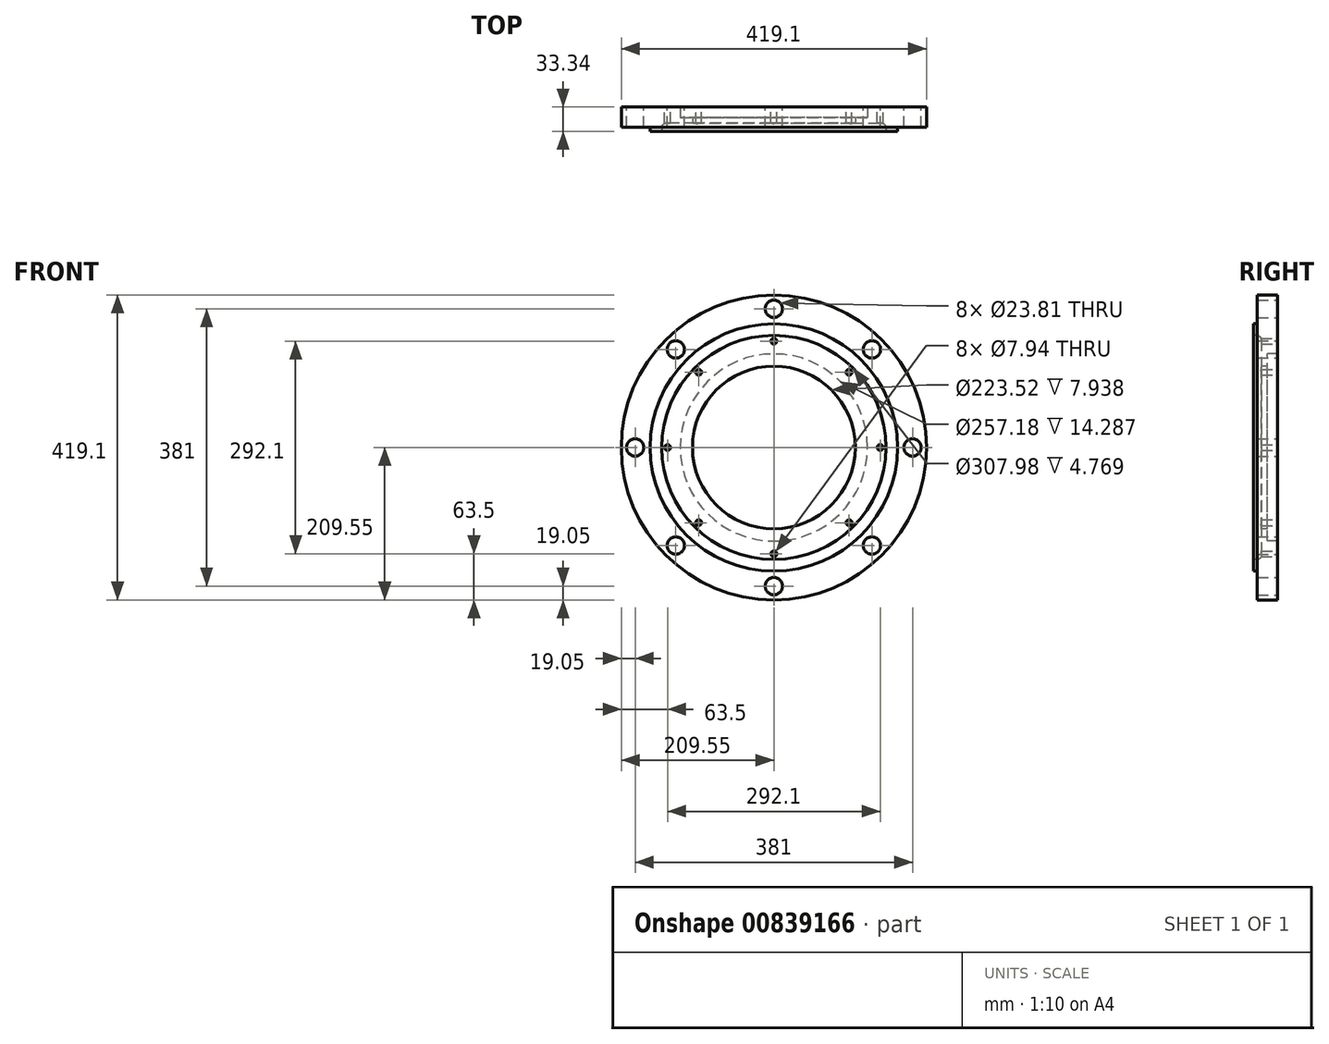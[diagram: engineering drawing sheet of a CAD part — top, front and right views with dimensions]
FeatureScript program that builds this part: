
annotation { "Feature Type Name" : "Feature", "Feature Type Description" : "" }
export const myFeature = defineFeature(function(context is Context, id is Id, definition is map)
    precondition{}
    {
        {
            var Q0;
            Q0=qCreatedBy(makeId("Right.planeOp"),FACE);
            var sketch = newSketch(context, id + "F0", { "sketchPlane" : qUnion([Q0])});
            skLineSegment(sketch, "E0", {"start": v(0, 209.55) * mm, "end": v(-27.78, 209.55) * mm});
            skLineSegment(sketch, "E1", {"start": v(-27.78, 209.55) * mm, "end": v(-27.78, 169.89) * mm});
            skLineSegment(sketch, "E2", {"start": v(-27.78, 169.89) * mm, "end": v(-33.34, 169.89) * mm});
            skLineSegment(sketch, "E3", {"start": v(-33.34, 169.89) * mm, "end": v(-33.34, 153.99) * mm});
            skLineSegment(sketch, "E4", {"start": v(-33.34, 153.99) * mm, "end": v(-28.57, 153.99) * mm});
            skLineSegment(sketch, "E5", {"start": v(-22.22, 147.64) * mm, "end": v(-22.22, 111.76) * mm});
            skLineSegment(sketch, "E6", {"start": v(-22.22, 111.76) * mm, "end": v(-14.29, 111.76) * mm});
            skLineSegment(sketch, "E7", {"start": v(-14.29, 111.76) * mm, "end": v(-14.29, 128.59) * mm});
            skLineSegment(sketch, "E8", {"start": v(-14.29, 128.59) * mm, "end": v(0, 128.59) * mm});
            skLineSegment(sketch, "E9", {"start": v(0, 128.59) * mm, "end": v(0, 209.55) * mm});
            skPoint(sketch, "E10.visualSharp", {"position": v(-22.22, 153.99) * mm});
            skArc(sketch, "E10.filletArc", {"start": v(-22.22, 147.64) * mm, "mid": v(-24.08, 152.13) * mm, "end": v(-28.57, 153.99) * mm});
            skLineSegment(sketch, "E11", {"start": v(0, 0) * mm, "end": v(181.13, 0) * mm});
            skSolve(sketch);
        }
        {
            var Q0;
            Q0=makeQuery(id+"F0.imprint","IMPRINT",FACE,{"disambiguationData":[TD([[makeQuery(id+"F0.imprint","IMPRINT",EDGE,{"derivedFrom":sQuery(id+"F0.wireOp",EDGE,"E0")}),1.0]])]});
            var Q1;
            Q1=sQuery(id+"F0.wireOp",EDGE,"E11");
            revolve(context, id + "F1", {"surfaceOperationType" : NewSurfaceOperationType.NEW, "entities" : qUnion([Q0]), "axis" : qUnion([Q1]), "revolveType" : RevolveType.FULL});
        }
        {
            var Q0;
            Q0=makeQuery(id+"F1.opRevolve","SWEPT_EDGE",EDGE,{"disambiguationData":[OSD([sQuery(id+"F0.wireOp",EDGE,"E1"),sQuery(id+"F0.wireOp",EDGE,"E2")])]});
            fillet(context, id + "F2", {"entities" : qUnion([Q0]), "radius" : 1.59 * mm, "tangentPropagation" : true, "allowEdgeOverflow" : false});
        }
        {
            var Q0;
            Q0=makeQuery(id+"F1.opRevolve","SWEPT_FACE",FACE,{"disambiguationData":[OSD([sQuery(id+"F0.wireOp",EDGE,"E9")])]});
            var sketch = newSketch(context, id + "F3", { "sketchPlane" : qUnion([Q0])});
            skCircle(sketch, "E12", {"center": v(0, 190.5) * mm, "radius": 11.9 * mm});
            skCircle(sketch, "E13.1.0", {"center": v(-134.7, 134.7) * mm, "radius": 11.9 * mm});
            skCircle(sketch, "E13.2.0", {"center": v(-190.5, 0) * mm, "radius": 11.9 * mm});
            skCircle(sketch, "E13.3.0", {"center": v(-134.7, -134.7) * mm, "radius": 11.9 * mm});
            skCircle(sketch, "E13.4.0", {"center": v(0, -190.5) * mm, "radius": 11.9 * mm});
            skCircle(sketch, "E13.5.0", {"center": v(134.7, -134.7) * mm, "radius": 11.9 * mm});
            skCircle(sketch, "E13.6.0", {"center": v(190.5, 0) * mm, "radius": 11.9 * mm});
            skCircle(sketch, "E13.7.0", {"center": v(134.7, 134.7) * mm, "radius": 11.9 * mm});
            skPoint(sketch, "E13.center", {"position": v(0, 0) * mm});
            skSolve(sketch);
        }
        {
            var Q0;
            Q0 = qSketchRegion(id + "F3", true);
            extrude(context, id + "F4", {"entities" : qUnion([Q0]), "operationType" : NewBodyOperationType.REMOVE, "endBound" : BoundingType.UP_TO_NEXT, "oppositeDirection" : true, "depth" : 25.4 * mm, "offsetDistance" : 25.4 * mm});
        }
        {
            var Q0;
            Q0=makeQuery(id+"F1.opRevolve","SWEPT_FACE",FACE,{"disambiguationData":[OSD([sQuery(id+"F0.wireOp",EDGE,"E9")])]});
            var sketch = newSketch(context, id + "F5", { "sketchPlane" : qUnion([Q0])});
            skCircle(sketch, "E14", {"center": v(0, 146.05) * mm, "radius": 3.97 * mm});
            skCircle(sketch, "E15.1.0", {"center": v(-103.27, 103.27) * mm, "radius": 3.97 * mm});
            skCircle(sketch, "E15.2.0", {"center": v(-146.05, 0) * mm, "radius": 3.97 * mm});
            skCircle(sketch, "E15.3.0", {"center": v(-103.27, -103.27) * mm, "radius": 3.97 * mm});
            skCircle(sketch, "E15.4.0", {"center": v(0, -146.05) * mm, "radius": 3.97 * mm});
            skCircle(sketch, "E15.5.0", {"center": v(103.27, -103.27) * mm, "radius": 3.97 * mm});
            skCircle(sketch, "E15.6.0", {"center": v(146.05, 0) * mm, "radius": 3.97 * mm});
            skCircle(sketch, "E15.7.0", {"center": v(103.27, 103.27) * mm, "radius": 3.97 * mm});
            skPoint(sketch, "E15.center", {"position": v(0, 0) * mm});
            skSolve(sketch);
        }
        {
            var Q0;
            Q0 = qSketchRegion(id + "F5", true);
            extrude(context, id + "F6", {"entities" : qUnion([Q0]), "operationType" : NewBodyOperationType.REMOVE, "endBound" : BoundingType.UP_TO_NEXT, "oppositeDirection" : true, "depth" : 25.4 * mm, "offsetDistance" : 25.4 * mm});
        }
    });
